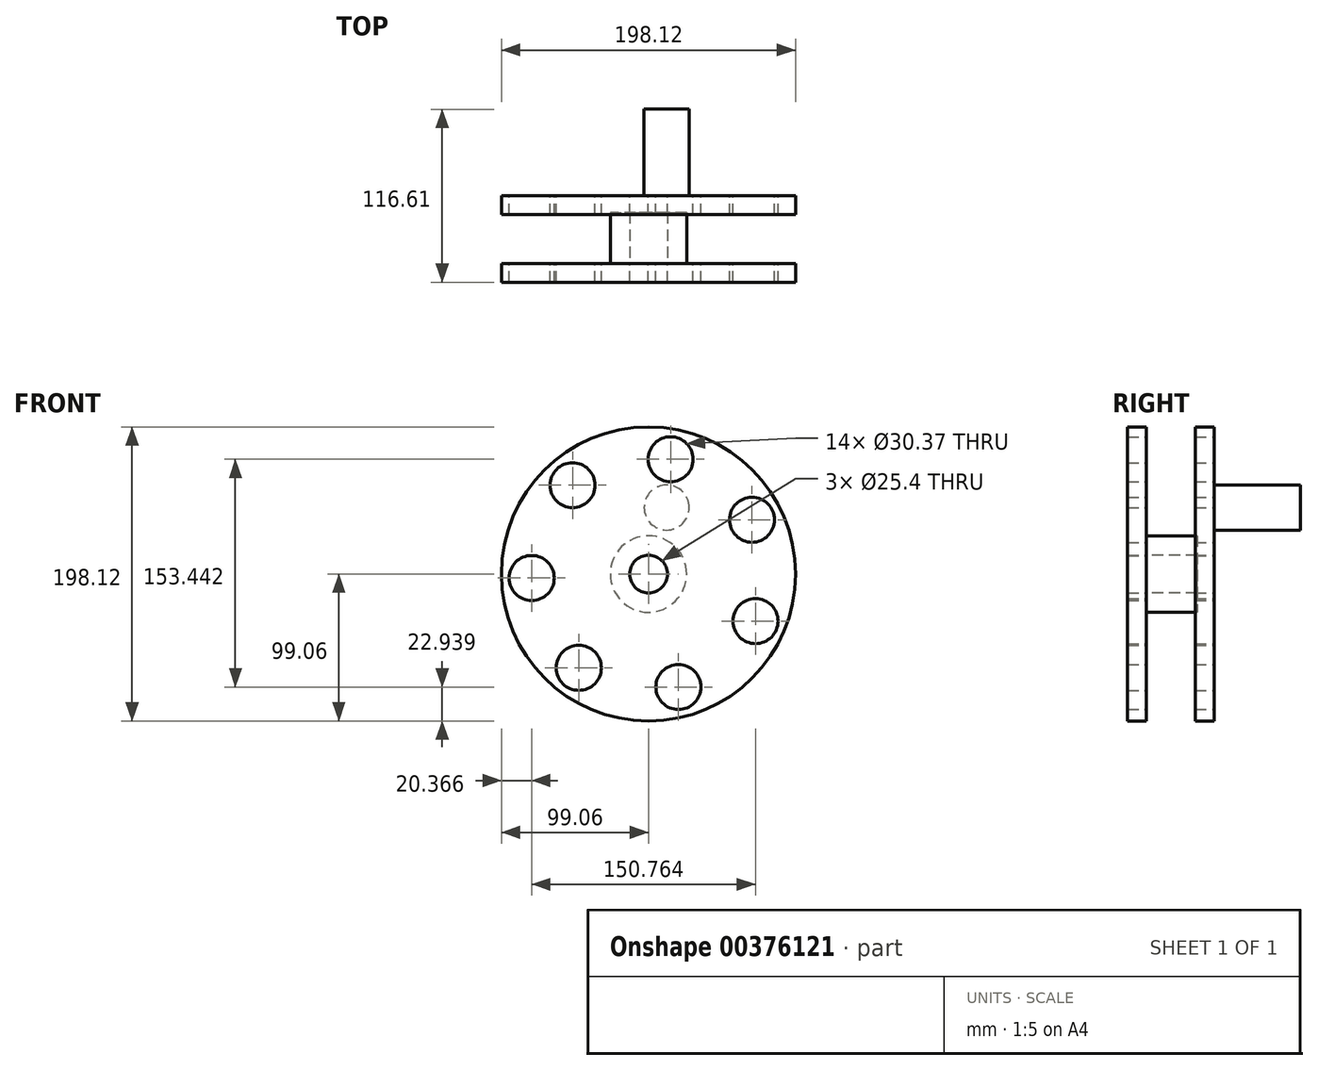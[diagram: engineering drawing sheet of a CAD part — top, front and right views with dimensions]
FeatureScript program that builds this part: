
annotation { "Feature Type Name" : "Feature", "Feature Type Description" : "" }
export const myFeature = defineFeature(function(context is Context, id is Id, definition is map)
    precondition{}
    {
        {
            var Q0;
            Q0=qCreatedBy(makeId("Front.planeOp"),FACE);
            var sketch = newSketch(context, id + "F0", { "sketchPlane" : qUnion([Q0])});
            skCircle(sketch, "E0", {"center": v(0, 0) * mm, "radius": 99.06 * mm});
            skCircle(sketch, "E1.cCircle", {"center": v(0, 0) * mm, "radius": 70.94 * mm, "construction": true});
            skLineSegment(sketch, "E1.0", {"start": v(72.07, -31.72) * mm, "end": v(20.14, -76.12) * mm});
            skLineSegment(sketch, "E1.1", {"start": v(20.14, -76.12) * mm, "end": v(-46.96, -63.2) * mm});
            skLineSegment(sketch, "E1.2", {"start": v(-46.96, -63.2) * mm, "end": v(-78.7, -2.7) * mm});
            skLineSegment(sketch, "E1.3", {"start": v(-78.7, -2.7) * mm, "end": v(-51.17, 59.85) * mm});
            skLineSegment(sketch, "E1.4", {"start": v(-51.17, 59.85) * mm, "end": v(14.88, 77.32) * mm});
            skLineSegment(sketch, "E1.5", {"start": v(14.88, 77.32) * mm, "end": v(69.73, 36.57) * mm});
            skLineSegment(sketch, "E1.6", {"start": v(69.73, 36.57) * mm, "end": v(72.07, -31.72) * mm});
            skPoint(sketch, "E1.0.midPoint", {"position": v(46.1, -53.92) * mm});
            skCircle(sketch, "E2", {"center": v(-51.17, 59.85) * mm, "radius": 15.18 * mm});
            skCircle(sketch, "E3", {"center": v(14.88, 77.32) * mm, "radius": 15.18 * mm});
            skCircle(sketch, "E4", {"center": v(69.73, 36.57) * mm, "radius": 15.18 * mm});
            skCircle(sketch, "E5", {"center": v(72.07, -31.72) * mm, "radius": 15.18 * mm});
            skCircle(sketch, "E6", {"center": v(20.14, -76.12) * mm, "radius": 15.18 * mm});
            skCircle(sketch, "E7", {"center": v(-46.96, -63.2) * mm, "radius": 15.18 * mm});
            skCircle(sketch, "E8", {"center": v(-78.7, -2.7) * mm, "radius": 15.18 * mm});
            skCircle(sketch, "E9", {"center": v(0, 0) * mm, "radius": 12.7 * mm});
            skSolve(sketch);
        }
        {
            var Q0;
            Q0=makeQuery(id+"F0.imprint","IMPRINT",FACE,{"disambiguationData":[TD([[makeQuery(id+"F0.imprint","IMPRINT",EDGE,{"derivedFrom":sQuery(id+"F0.wireOp",EDGE,"E0")}),1.0]])]});
            var Q1;
            Q1=makeQuery(id+"F0.imprint","IMPRINT",FACE,{"disambiguationData":[TD([[makeQuery(id+"F0.imprint","IMPRINT",EDGE,{"derivedFrom":sQuery(id+"F0.wireOp",EDGE,"E9")}),-1.0]])]});
            extrude(context, id + "F1", {"entities" : qUnion([Q0, Q1]), "depth" : 12.7 * mm});
        }
        {
            var Q0;
            Q0=makeQuery(id+"F1.opExtrude","SWEPT_BODY",BODY,{"disambiguationData":[OSD([sQuery(id+"F0.wireOp",EDGE,"E0"),sQuery(id+"F0.wireOp",EDGE,"E2"),sQuery(id+"F0.wireOp",EDGE,"E3"),sQuery(id+"F0.wireOp",EDGE,"E4"),sQuery(id+"F0.wireOp",EDGE,"E5"),sQuery(id+"F0.wireOp",EDGE,"E6"),sQuery(id+"F0.wireOp",EDGE,"E7"),sQuery(id+"F0.wireOp",EDGE,"E8"),sQuery(id+"F0.wireOp",EDGE,"E9")])]});
            var Q1;
            Q1=makeQuery(id+"F1.opExtrude","CAP_FACE",FACE,{"disambiguationData":[OSD([sQuery(id+"F0.wireOp",EDGE,"E0"),sQuery(id+"F0.wireOp",EDGE,"E2"),sQuery(id+"F0.wireOp",EDGE,"E3"),sQuery(id+"F0.wireOp",EDGE,"E4"),sQuery(id+"F0.wireOp",EDGE,"E5"),sQuery(id+"F0.wireOp",EDGE,"E6"),sQuery(id+"F0.wireOp",EDGE,"E7"),sQuery(id+"F0.wireOp",EDGE,"E8"),sQuery(id+"F0.wireOp",EDGE,"E9")])],"isStart":true});
            transform(context, id + "F2", {"entities" : qUnion([Q0]), "transformType" : TransformType.TRANSLATION_DISTANCE, "transformDirection" : qUnion([Q1]), "distance" : 30.37 * mm, "makeCopy" : true});
        }
        {
            var Q0;
            Q0=makeQuery(id+"F2.opPattern","COPY",BODY,{"derivedFrom":makeQuery(id+"F1.opExtrude","SWEPT_BODY",BODY,{"disambiguationData":[OSD([sQuery(id+"F0.wireOp",EDGE,"E0"),sQuery(id+"F0.wireOp",EDGE,"E2"),sQuery(id+"F0.wireOp",EDGE,"E3"),sQuery(id+"F0.wireOp",EDGE,"E4"),sQuery(id+"F0.wireOp",EDGE,"E5"),sQuery(id+"F0.wireOp",EDGE,"E6"),sQuery(id+"F0.wireOp",EDGE,"E7"),sQuery(id+"F0.wireOp",EDGE,"E8"),sQuery(id+"F0.wireOp",EDGE,"E9")])]}),"instanceName":"1"});
            var Q1;
            Q1=makeQuery(id+"F1.opExtrude","CAP_FACE",FACE,{"disambiguationData":[OSD([sQuery(id+"F0.wireOp",EDGE,"E0"),sQuery(id+"F0.wireOp",EDGE,"E2"),sQuery(id+"F0.wireOp",EDGE,"E3"),sQuery(id+"F0.wireOp",EDGE,"E4"),sQuery(id+"F0.wireOp",EDGE,"E5"),sQuery(id+"F0.wireOp",EDGE,"E6"),sQuery(id+"F0.wireOp",EDGE,"E7"),sQuery(id+"F0.wireOp",EDGE,"E8"),sQuery(id+"F0.wireOp",EDGE,"E9")])],"isStart":true});
            transform(context, id + "F3", {"entities" : qUnion([Q0]), "transformType" : TransformType.TRANSLATION_DISTANCE, "transformDirection" : qUnion([Q1]), "distance" : 15.24 * mm, "makeCopy" : false});
        }
        {
            var Q0;
            Q0=makeQuery(id+"F1.opExtrude","CAP_FACE",FACE,{"disambiguationData":[OSD([sQuery(id+"F0.wireOp",EDGE,"E0"),sQuery(id+"F0.wireOp",EDGE,"E2"),sQuery(id+"F0.wireOp",EDGE,"E3"),sQuery(id+"F0.wireOp",EDGE,"E4"),sQuery(id+"F0.wireOp",EDGE,"E5"),sQuery(id+"F0.wireOp",EDGE,"E6"),sQuery(id+"F0.wireOp",EDGE,"E7"),sQuery(id+"F0.wireOp",EDGE,"E8"),sQuery(id+"F0.wireOp",EDGE,"E9")])],"isStart":true});
            var sketch = newSketch(context, id + "F4", { "sketchPlane" : qUnion([Q0])});
            skCircle(sketch, "E10", {"center": v(0, 0) * mm, "radius": 25.75 * mm});
            skSolve(sketch);
        }
        {
            var Q0;
            Q0=makeQuery(id+"F4.imprint","IMPRINT",FACE,{"disambiguationData":[TD([[makeQuery(id+"F4.imprint","IMPRINT",EDGE,{"derivedFrom":sQuery(id+"F4.wireOp",EDGE,"E10")}),1.0]])]});
            extrude(context, id + "F5", {"entities" : qUnion([Q0]), "depth" : 34.3 * mm});
        }
        {
            var Q0;
            Q0=makeQuery(id+"F2.opPattern","COPY",FACE,{"derivedFrom":makeQuery(id+"F1.opExtrude","CAP_FACE",FACE,{"disambiguationData":[OSD([sQuery(id+"F0.wireOp",EDGE,"E0"),sQuery(id+"F0.wireOp",EDGE,"E2"),sQuery(id+"F0.wireOp",EDGE,"E3"),sQuery(id+"F0.wireOp",EDGE,"E4"),sQuery(id+"F0.wireOp",EDGE,"E5"),sQuery(id+"F0.wireOp",EDGE,"E6"),sQuery(id+"F0.wireOp",EDGE,"E7"),sQuery(id+"F0.wireOp",EDGE,"E8"),sQuery(id+"F0.wireOp",EDGE,"E9")])],"isStart":true}),"instanceName":"1"});
            var sketch = newSketch(context, id + "F6", { "sketchPlane" : qUnion([Q0])});
            skCircle(sketch, "E11", {"center": v(-12.23, 44.8) * mm, "radius": 15.18 * mm});
            skSolve(sketch);
        }
        {
            var Q0;
            Q0=makeQuery(id+"F6.imprint","IMPRINT",FACE,{"disambiguationData":[TD([[makeQuery(id+"F6.imprint","IMPRINT",EDGE,{"derivedFrom":sQuery(id+"F6.wireOp",EDGE,"E11")}),1.0]])]});
            extrude(context, id + "F7", {"entities" : qUnion([Q0]), "depth" : 58.3 * mm});
        }
    });
